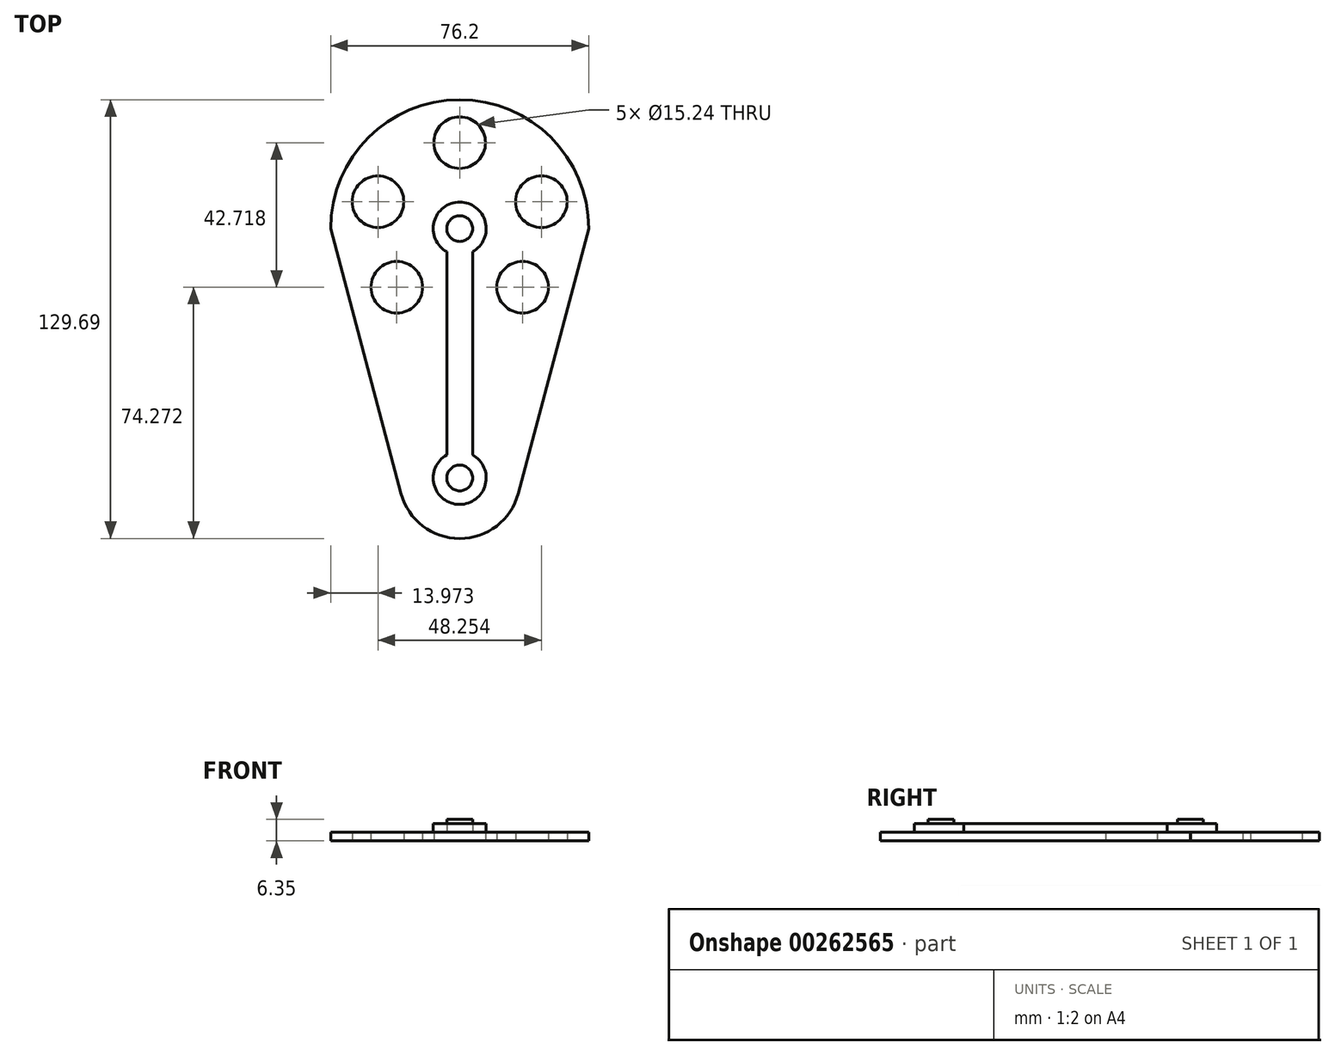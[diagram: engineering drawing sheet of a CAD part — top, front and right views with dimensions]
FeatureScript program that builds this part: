
annotation { "Feature Type Name" : "Feature", "Feature Type Description" : "" }
export const myFeature = defineFeature(function(context is Context, id is Id, definition is map)
    precondition{}
    {
        {
            var Q0;
            Q0=qCreatedBy(makeId("Top.planeOp"),FACE);
            var sketch = newSketch(context, id + "F0", { "sketchPlane" : qUnion([Q0])});
            skLineSegment(sketch, "E0", {"start": v(0, 0) * mm, "end": v(0, 25.4) * mm, "construction": true});
            skCircle(sketch, "E1", {"center": v(0, 25.4) * mm, "radius": 7.62 * mm});
            skLineSegment(sketch, "E2", {"start": v(0, 0) * mm, "end": v(-24.13, 7.94) * mm, "construction": true});
            skLineSegment(sketch, "E3", {"start": v(-38.1, 0) * mm, "end": v(-17.3, -78.28) * mm});
            skLineSegment(sketch, "E4.MirrorCS", {"start": v(38.1, 0) * mm, "end": v(17.3, -78.28) * mm});
            skArc(sketch, "E5.trimOffspring", {"start": v(38.1, 0) * mm, "mid": v(0, 38.1) * mm, "end": v(-38.1, 0) * mm});
            skCircle(sketch, "E6", {"center": v(-24.13, 7.94) * mm, "radius": 7.62 * mm});
            skCircle(sketch, "E7.MirrorC", {"center": v(24.13, 7.94) * mm, "radius": 7.62 * mm});
            skLineSegment(sketch, "E8", {"start": v(0, 0) * mm, "end": v(-18.58, -17.32) * mm, "construction": true});
            skCircle(sketch, "E9", {"center": v(-18.58, -17.32) * mm, "radius": 7.62 * mm});
            skCircle(sketch, "E10.MirrorC", {"center": v(18.58, -17.32) * mm, "radius": 7.62 * mm});
            skCircle(sketch, "E11", {"center": v(0, 0) * mm, "radius": 7.82 * mm});
            skArc(sketch, "E12", {"start": v(-17.3, -78.28) * mm, "mid": v(0, -91.6) * mm, "end": v(17.3, -78.28) * mm});
            skCircle(sketch, "E13", {"center": v(0, -73.68) * mm, "radius": 7.82 * mm});
            skLineSegment(sketch, "E14", {"start": v(-3.81, -6.83) * mm, "end": v(-3.81, -66.85) * mm});
            skLineSegment(sketch, "E15.MirrorCS", {"start": v(3.81, -6.83) * mm, "end": v(3.81, -66.85) * mm});
            skCircle(sketch, "E16", {"center": v(0, 0) * mm, "radius": 3.81 * mm});
            skCircle(sketch, "E17", {"center": v(0, -73.68) * mm, "radius": 3.81 * mm});
            skSolve(sketch);
        }
        {
            var Q0;
            Q0=makeQuery(id+"F0.imprint","IMPRINT",FACE,{"disambiguationData":[TD([[makeQuery(id+"F0.imprint","IMPRINT",EDGE,{"derivedFrom":sQuery(id+"F0.wireOp",EDGE,"E1")}),-1.0]])]});
            extrude(context, id + "F1", {"entities" : qUnion([Q0]), "depth" : 2.54 * mm});
        }
        {
            var Q0;
            {var subQ0=sQuery(id+"F0.wireOp",EDGE,"E14");Q0=makeQuery(id+"F0.imprint","IMPRINT",FACE,{"disambiguationData":[TD([[makeQuery(id+"F0.imprint","IMPRINT",EDGE,{"derivedFrom":subQ0}),1.0]])]});}
            var Q1;
            {var subQ0=sQuery(id+"F0.wireOp",EDGE,"E13");var subQ1=makeQuery(id+"F0.imprint","INTERSECT",VERTEX,{"derivedFrom":[subQ0,sQuery(id+"F0.wireOp",EDGE,"E14")]});Q1=makeQuery(id+"F0.imprint","IMPRINT",FACE,{"disambiguationData":[TD([[makeQuery(id+"F0.imprint","IMPRINT",EDGE,{"disambiguationData":[TD([[subQ1,1.0]])],"derivedFrom":subQ0}),1.0]])]});}
            var Q2;
            {var subQ0=sQuery(id+"F0.wireOp",EDGE,"E11");var subQ1=makeQuery(id+"F0.imprint","INTERSECT",VERTEX,{"derivedFrom":[subQ0,sQuery(id+"F0.wireOp",EDGE,"E14")]});Q2=makeQuery(id+"F0.imprint","IMPRINT",FACE,{"disambiguationData":[TD([[makeQuery(id+"F0.imprint","IMPRINT",EDGE,{"disambiguationData":[TD([[subQ1,-1.0]])],"derivedFrom":subQ0}),1.0]])]});}
            extrude(context, id + "F2", {"entities" : qUnion([Q0, Q1, Q2]), "operationType" : NewBodyOperationType.ADD, "depth" : 5.08 * mm});
        }
        {
            var Q0;
            Q0=makeQuery(id+"F0.imprint","IMPRINT",FACE,{"disambiguationData":[TD([[makeQuery(id+"F0.imprint","IMPRINT",EDGE,{"derivedFrom":sQuery(id+"F0.wireOp",EDGE,"E17")}),1.0]])]});
            var Q1;
            Q1=makeQuery(id+"F0.imprint","IMPRINT",FACE,{"disambiguationData":[TD([[makeQuery(id+"F0.imprint","IMPRINT",EDGE,{"derivedFrom":sQuery(id+"F0.wireOp",EDGE,"E16")}),1.0]])]});
            extrude(context, id + "F3", {"entities" : qUnion([Q0, Q1]), "operationType" : NewBodyOperationType.ADD, "depth" : 6.35 * mm});
        }
    });
